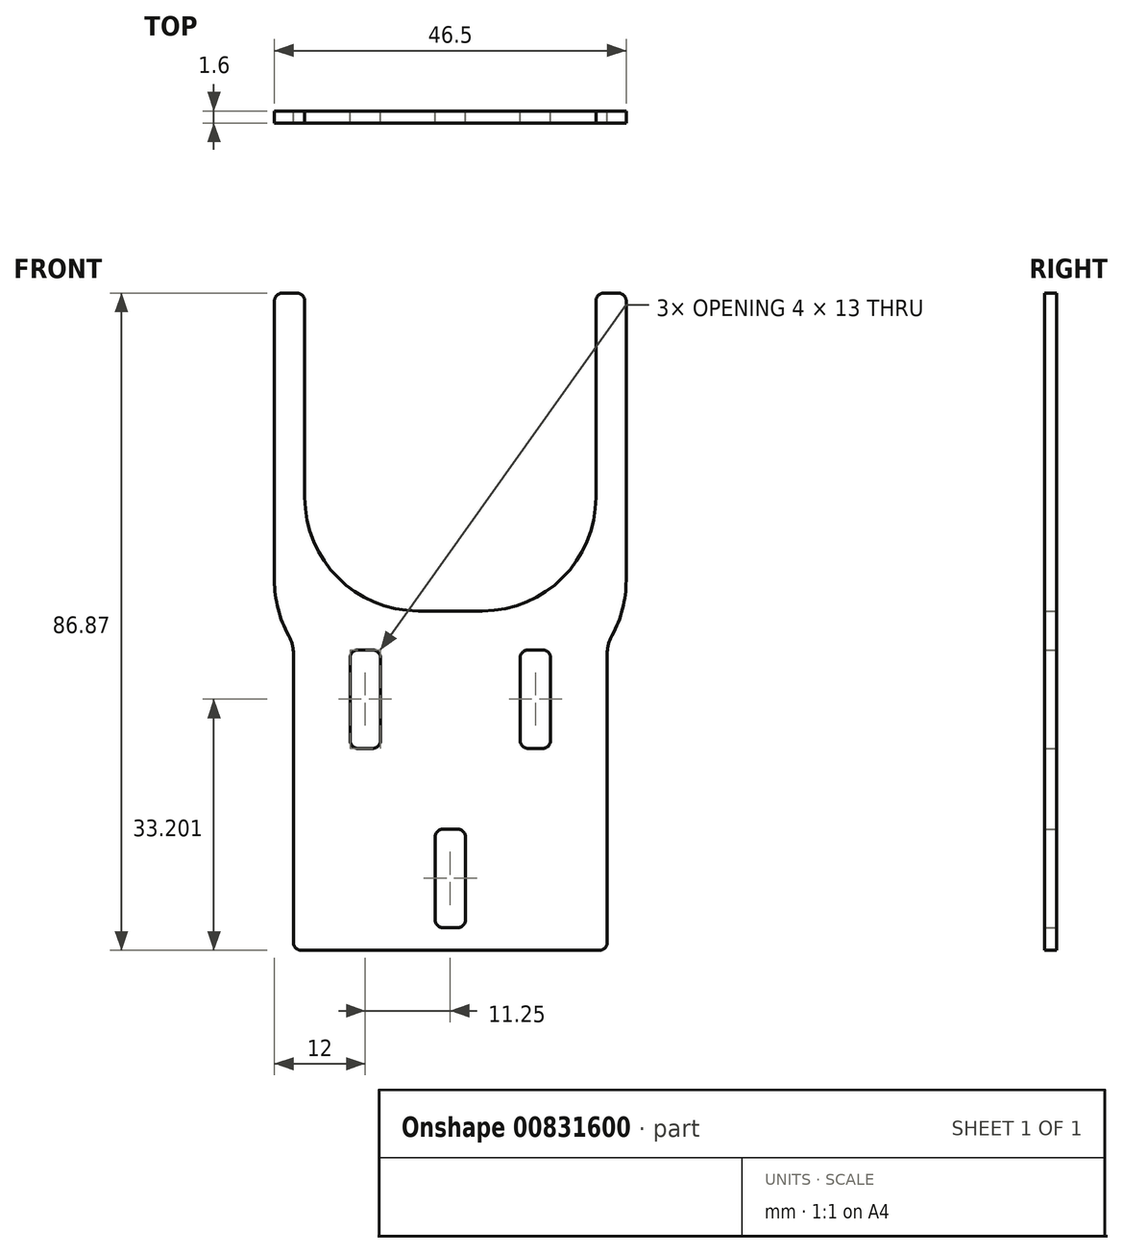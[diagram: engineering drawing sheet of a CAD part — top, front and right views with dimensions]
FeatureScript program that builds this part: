
annotation { "Feature Type Name" : "Feature", "Feature Type Description" : "" }
export const myFeature = defineFeature(function(context is Context, id is Id, definition is map)
    precondition{}
    {
        {
            var Q0;
            Q0=qCreatedBy(makeId("Front.planeOp"),FACE);
            var sketch = newSketch(context, id + "F0", { "sketchPlane" : qUnion([Q0])});
            skLineSegment(sketch, "E0.top", {"start": v(-23.25, 42) * mm, "end": v(-19.25, 42) * mm});
            skLineSegment(sketch, "E0.left", {"start": v(-23.25, 0) * mm, "end": v(-23.25, 42) * mm});
            skLineSegment(sketch, "E0.right", {"start": v(23.25, 0) * mm, "end": v(23.25, 42) * mm});
            skLineSegment(sketch, "E1", {"start": v(-19.25, 42) * mm, "end": v(-19.25, 0) * mm});
            skLineSegment(sketch, "E2", {"start": v(19.25, 42) * mm, "end": v(19.25, 0) * mm});
            skLineSegment(sketch, "E3.top", {"start": v(-20.75, -44.87) * mm, "end": v(20.75, -44.87) * mm});
            skLineSegment(sketch, "E3.right", {"start": v(20.75, -4.33) * mm, "end": v(20.75, -44.87) * mm});
            skLineSegment(sketch, "E4.bottom", {"start": v(-13.25, -5.17) * mm, "end": v(-9.25, -5.17) * mm});
            skLineSegment(sketch, "E4.top", {"start": v(-13.25, -18.17) * mm, "end": v(-9.25, -18.17) * mm});
            skLineSegment(sketch, "E4.left", {"start": v(-13.25, -5.17) * mm, "end": v(-13.25, -18.17) * mm});
            skLineSegment(sketch, "E4.right", {"start": v(-9.25, -5.17) * mm, "end": v(-9.25, -18.17) * mm});
            skLineSegment(sketch, "E5.bottom", {"start": v(9.25, -5.17) * mm, "end": v(13.25, -5.17) * mm});
            skLineSegment(sketch, "E5.top", {"start": v(9.25, -18.17) * mm, "end": v(13.25, -18.17) * mm});
            skLineSegment(sketch, "E5.left", {"start": v(9.25, -5.17) * mm, "end": v(9.25, -18.17) * mm});
            skLineSegment(sketch, "E5.right", {"start": v(13.25, -5.17) * mm, "end": v(13.25, -18.17) * mm});
            skLineSegment(sketch, "E6.bottom", {"start": v(-2, -28.87) * mm, "end": v(2, -28.87) * mm});
            skLineSegment(sketch, "E6.top", {"start": v(-2, -41.87) * mm, "end": v(2, -41.87) * mm});
            skLineSegment(sketch, "E6.left", {"start": v(-2, -28.87) * mm, "end": v(-2, -41.87) * mm});
            skLineSegment(sketch, "E6.right", {"start": v(2, -28.87) * mm, "end": v(2, -41.87) * mm});
            skPoint(sketch, "E7", {"position": v(0, -44.87) * mm});
            skPoint(sketch, "E8", {"position": v(0, -41.87) * mm});
            skPoint(sketch, "E9", {"position": v(0, 42) * mm});
            skPoint(sketch, "E10", {"position": v(0, 0) * mm});
            skLineSegment(sketch, "E11", {"start": v(-20.75, -4.33) * mm, "end": v(-20.75, -44.87) * mm});
            skLineSegment(sketch, "E12.trimOffspring", {"start": v(19.25, 42) * mm, "end": v(23.25, 42) * mm});
            skLineSegment(sketch, "E13.trimOffspring", {"start": v(-19.25, 0) * mm, "end": v(19.25, 0) * mm});
            skLineSegment(sketch, "E14", {"start": v(20.75, -4.33) * mm, "end": v(23.25, 0) * mm});
            skLineSegment(sketch, "E15", {"start": v(-20.75, -4.33) * mm, "end": v(-23.25, 0) * mm});
            skSolve(sketch);
        }
        {
            var Q0;
            {var subQ0=sQuery(id+"F0.wireOp",EDGE,"E3.top");Q0=makeQuery(id+"F0.imprint","IMPRINT",FACE,{"disambiguationData":[TD([[makeQuery(id+"F0.imprint","IMPRINT",EDGE,{"derivedFrom":subQ0}),1.0]])]});}
            var Q1;
            {var subQ4=sQuery(id+"F0.wireOp",EDGE,"E0.top");Q1=makeQuery(id+"F0.imprint","IMPRINT",FACE,{"disambiguationData":[TD([[makeQuery(id+"F0.imprint","IMPRINT",EDGE,{"derivedFrom":subQ4}),-1.0]])]});}
            var Q2;
            {var subQ3=sQuery(id+"F0.wireOp",EDGE,"QKQ0wrBP-9eUS-REHq-0FP2-Jo7S615HdIO2");Q2=makeQuery(id+"F0.imprint","IMPRINT",FACE,{"disambiguationData":[TD([[makeQuery(id+"F0.imprint","IMPRINT",EDGE,{"derivedFrom":subQ3}),-1.0]])]});}
            var Q3;
            {var subQ0=sQuery(id+"F0.wireOp",EDGE,"4tHI9naV-DgC1-T7u8-fLkl-fecvC8TNhq8U");Q3=makeQuery(id+"F0.imprint","IMPRINT",FACE,{"disambiguationData":[TD([[makeQuery(id+"F0.imprint","IMPRINT",EDGE,{"derivedFrom":subQ0}),1.0]])]});}
            var Q4;
            {var subQ1=sQuery(id+"F0.wireOp",EDGE,"E0.right");Q4=makeQuery(id+"F0.imprint","IMPRINT",FACE,{"disambiguationData":[TD([[makeQuery(id+"F0.imprint","IMPRINT",EDGE,{"derivedFrom":subQ1}),1.0]])]});}
            var Q5;
            {var subQ3=sQuery(id+"F0.wireOp",EDGE,"YY5VN5UC-LBhe-GtBM-lLEQ-fAFLk2ytWkNk");Q5=makeQuery(id+"F0.imprint","IMPRINT",FACE,{"disambiguationData":[TD([[makeQuery(id+"F0.imprint","IMPRINT",EDGE,{"derivedFrom":subQ3}),1.0]])]});}
            var Q6;
            {var subQ3=sQuery(id+"F0.wireOp",EDGE,"cMXV6rv2-uTEe-Yukd-aD0D-mM5V33J1QYcm");Q6=makeQuery(id+"F0.imprint","IMPRINT",FACE,{"disambiguationData":[TD([[makeQuery(id+"F0.imprint","IMPRINT",EDGE,{"derivedFrom":subQ3}),-1.0]])]});}
            extrude(context, id + "F1", {"entities" : qUnion([Q0, Q1, Q2, Q3, Q4, Q5, Q6]), "depth" : 1.6 * mm, "offsetDistance" : 25 * mm});
        }
        {
            var Q0;
            Q0=makeQuery(id+"F1.opExtrude","SWEPT_EDGE",EDGE,{"disambiguationData":[OSD([sQuery(id+"F0.wireOp",EDGE,"E1"),sQuery(id+"F0.wireOp",EDGE,"E13.trimOffspring")])]});
            var Q1;
            Q1=makeQuery(id+"F1.opExtrude","SWEPT_EDGE",EDGE,{"disambiguationData":[OSD([sQuery(id+"F0.wireOp",EDGE,"E2"),sQuery(id+"F0.wireOp",EDGE,"E13.trimOffspring")])]});
            var Q2;
            Q2=makeQuery(id+"F1.opExtrude","SWEPT_EDGE",EDGE,{"disambiguationData":[OSD([sQuery(id+"F0.wireOp",EDGE,"E0.right"),sQuery(id+"F0.wireOp",EDGE,"E14")])]});
            var Q3;
            Q3=makeQuery(id+"F1.opExtrude","SWEPT_EDGE",EDGE,{"disambiguationData":[OSD([sQuery(id+"F0.wireOp",EDGE,"E0.left"),sQuery(id+"F0.wireOp",EDGE,"E15")])]});
            fillet(context, id + "F2", {"entities" : qUnion([Q0, Q1, Q2, Q3]), "radius" : 15 * mm, "tangentPropagation" : true, "allowEdgeOverflow" : false});
        }
        {
            var Q0;
            Q0=makeQuery(id+"F1.opExtrude","SWEPT_EDGE",EDGE,{"disambiguationData":[OSD([sQuery(id+"F0.wireOp",EDGE,"E11"),sQuery(id+"F0.wireOp",EDGE,"E15")])]});
            var Q1;
            Q1=makeQuery(id+"F1.opExtrude","SWEPT_EDGE",EDGE,{"disambiguationData":[OSD([sQuery(id+"F0.wireOp",EDGE,"E3.right"),sQuery(id+"F0.wireOp",EDGE,"E14")])]});
            fillet(context, id + "F3", {"entities" : qUnion([Q0, Q1]), "radius" : 5 * mm, "tangentPropagation" : true, "allowEdgeOverflow" : false});
        }
        {
            var Q0;
            Q0=makeQuery(id+"F1.opExtrude","SWEPT_EDGE",EDGE,{"disambiguationData":[OSD([sQuery(id+"F0.wireOp",EDGE,"E4.bottom"),sQuery(id+"F0.wireOp",EDGE,"E4.left")])]});
            var Q1;
            Q1=makeQuery(id+"F1.opExtrude","SWEPT_EDGE",EDGE,{"disambiguationData":[OSD([sQuery(id+"F0.wireOp",EDGE,"E4.top"),sQuery(id+"F0.wireOp",EDGE,"E4.left")])]});
            var Q2;
            Q2=makeQuery(id+"F1.opExtrude","SWEPT_EDGE",EDGE,{"disambiguationData":[OSD([sQuery(id+"F0.wireOp",EDGE,"E4.bottom"),sQuery(id+"F0.wireOp",EDGE,"E4.right")])]});
            var Q3;
            Q3=makeQuery(id+"F1.opExtrude","SWEPT_EDGE",EDGE,{"disambiguationData":[OSD([sQuery(id+"F0.wireOp",EDGE,"E4.top"),sQuery(id+"F0.wireOp",EDGE,"E4.right")])]});
            var Q4;
            Q4=makeQuery(id+"F1.opExtrude","SWEPT_EDGE",EDGE,{"disambiguationData":[OSD([sQuery(id+"F0.wireOp",EDGE,"E5.top"),sQuery(id+"F0.wireOp",EDGE,"E5.right")])]});
            var Q5;
            Q5=makeQuery(id+"F1.opExtrude","SWEPT_EDGE",EDGE,{"disambiguationData":[OSD([sQuery(id+"F0.wireOp",EDGE,"E5.bottom"),sQuery(id+"F0.wireOp",EDGE,"E5.right")])]});
            var Q6;
            Q6=makeQuery(id+"F1.opExtrude","SWEPT_EDGE",EDGE,{"disambiguationData":[OSD([sQuery(id+"F0.wireOp",EDGE,"E5.bottom"),sQuery(id+"F0.wireOp",EDGE,"E5.left")])]});
            var Q7;
            Q7=makeQuery(id+"F1.opExtrude","SWEPT_EDGE",EDGE,{"disambiguationData":[OSD([sQuery(id+"F0.wireOp",EDGE,"E5.top"),sQuery(id+"F0.wireOp",EDGE,"E5.left")])]});
            var Q8;
            Q8=makeQuery(id+"F1.opExtrude","SWEPT_EDGE",EDGE,{"disambiguationData":[OSD([sQuery(id+"F0.wireOp",EDGE,"E6.top"),sQuery(id+"F0.wireOp",EDGE,"E6.left")])]});
            var Q9;
            Q9=makeQuery(id+"F1.opExtrude","SWEPT_EDGE",EDGE,{"disambiguationData":[OSD([sQuery(id+"F0.wireOp",EDGE,"E6.bottom"),sQuery(id+"F0.wireOp",EDGE,"E6.left")])]});
            var Q10;
            Q10=makeQuery(id+"F1.opExtrude","SWEPT_EDGE",EDGE,{"disambiguationData":[OSD([sQuery(id+"F0.wireOp",EDGE,"E6.bottom"),sQuery(id+"F0.wireOp",EDGE,"E6.right")])]});
            var Q11;
            Q11=makeQuery(id+"F1.opExtrude","SWEPT_EDGE",EDGE,{"disambiguationData":[OSD([sQuery(id+"F0.wireOp",EDGE,"E6.top"),sQuery(id+"F0.wireOp",EDGE,"E6.right")])]});
            var Q12;
            Q12=makeQuery(id+"F1.opExtrude","SWEPT_EDGE",EDGE,{"disambiguationData":[OSD([sQuery(id+"F0.wireOp",EDGE,"E3.top"),sQuery(id+"F0.wireOp",EDGE,"E3.right")])]});
            var Q13;
            Q13=makeQuery(id+"F1.opExtrude","SWEPT_EDGE",EDGE,{"disambiguationData":[OSD([sQuery(id+"F0.wireOp",EDGE,"E3.top"),sQuery(id+"F0.wireOp",EDGE,"E11")])]});
            var Q14;
            Q14=makeQuery(id+"F1.opExtrude","SWEPT_EDGE",EDGE,{"disambiguationData":[OSD([sQuery(id+"F0.wireOp",EDGE,"E0.top"),sQuery(id+"F0.wireOp",EDGE,"E1")])]});
            var Q15;
            Q15=makeQuery(id+"F1.opExtrude","SWEPT_EDGE",EDGE,{"disambiguationData":[OSD([sQuery(id+"F0.wireOp",EDGE,"E0.top"),sQuery(id+"F0.wireOp",EDGE,"E0.left")])]});
            var Q16;
            Q16=makeQuery(id+"F1.opExtrude","SWEPT_EDGE",EDGE,{"disambiguationData":[OSD([sQuery(id+"F0.wireOp",EDGE,"E2"),sQuery(id+"F0.wireOp",EDGE,"E12.trimOffspring")])]});
            var Q17;
            Q17=makeQuery(id+"F1.opExtrude","SWEPT_EDGE",EDGE,{"disambiguationData":[OSD([sQuery(id+"F0.wireOp",EDGE,"E0.right"),sQuery(id+"F0.wireOp",EDGE,"E12.trimOffspring")])]});
            fillet(context, id + "F4", {"entities" : qUnion([Q0, Q1, Q2, Q3, Q4, Q5, Q6, Q7, Q8, Q9, Q10, Q11, Q12, Q13, Q14, Q15, Q16, Q17]), "radius" : 1 * mm, "tangentPropagation" : true, "allowEdgeOverflow" : false});
        }
    });
